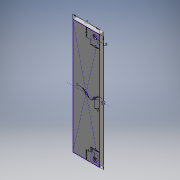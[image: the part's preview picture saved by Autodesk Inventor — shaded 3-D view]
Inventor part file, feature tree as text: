
AUTODESK INVENTOR PART (.ipt)
format: ipt  version: 2016 (Build 200138000, 138)  size: 111,616 bytes
history: native  units: mm
features: extrude x2
ambient origin geometry x8: Origin, YZ Plane, XZ Plane, XY Plane, X Axis, Y Axis, Z Axis, Center Point
bodies: Body1 (feature_tree)
feature tree (2):
  extrude  "押し出し2"  Depth=12.0mm
  extrude  "押し出し3"  Depth=52.0mm
